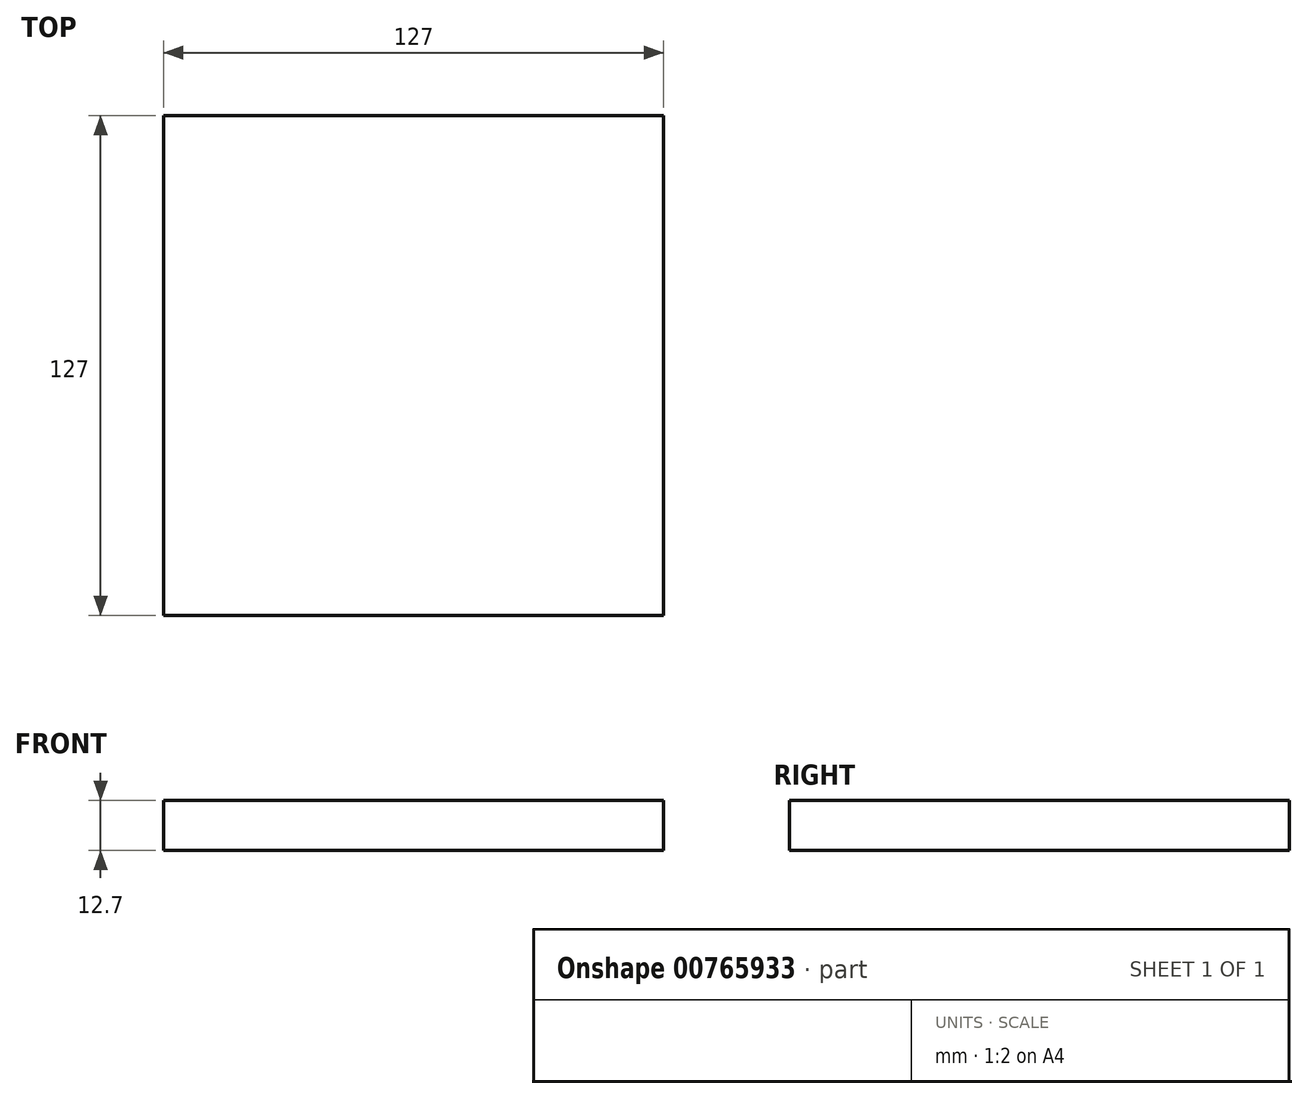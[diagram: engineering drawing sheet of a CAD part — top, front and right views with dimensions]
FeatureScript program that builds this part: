
annotation { "Feature Type Name" : "Feature", "Feature Type Description" : "" }
export const myFeature = defineFeature(function(context is Context, id is Id, definition is map)
    precondition{}
    {
        {
            var Q0;
            Q0=qCreatedBy(makeId("Top.planeOp"),FACE);
            var sketch = newSketch(context, id + "F0", { "sketchPlane" : qUnion([Q0])});
            skLineSegment(sketch, "E0.bottom", {"start": v(0, 0) * mm, "end": v(-127, 0) * mm});
            skLineSegment(sketch, "E0.top", {"start": v(0, 127) * mm, "end": v(-127, 127) * mm});
            skLineSegment(sketch, "E0.left", {"start": v(0, 0) * mm, "end": v(0, 127) * mm});
            skLineSegment(sketch, "E0.right", {"start": v(-127, 0) * mm, "end": v(-127, 127) * mm});
            skSolve(sketch);
        }
        {
            var Q0;
            Q0=makeQuery(id+"F0.imprint","IMPRINT",FACE,{"disambiguationData":[TD([[makeQuery(id+"F0.imprint","IMPRINT",EDGE,{"derivedFrom":sQuery(id+"F0.wireOp",EDGE,"E0.bottom")}),-1.0]])]});
            extrude(context, id + "F1", {"entities" : qUnion([Q0]), "depth" : 12.7 * mm, "offsetDistance" : 25.4 * mm});
        }
    });
